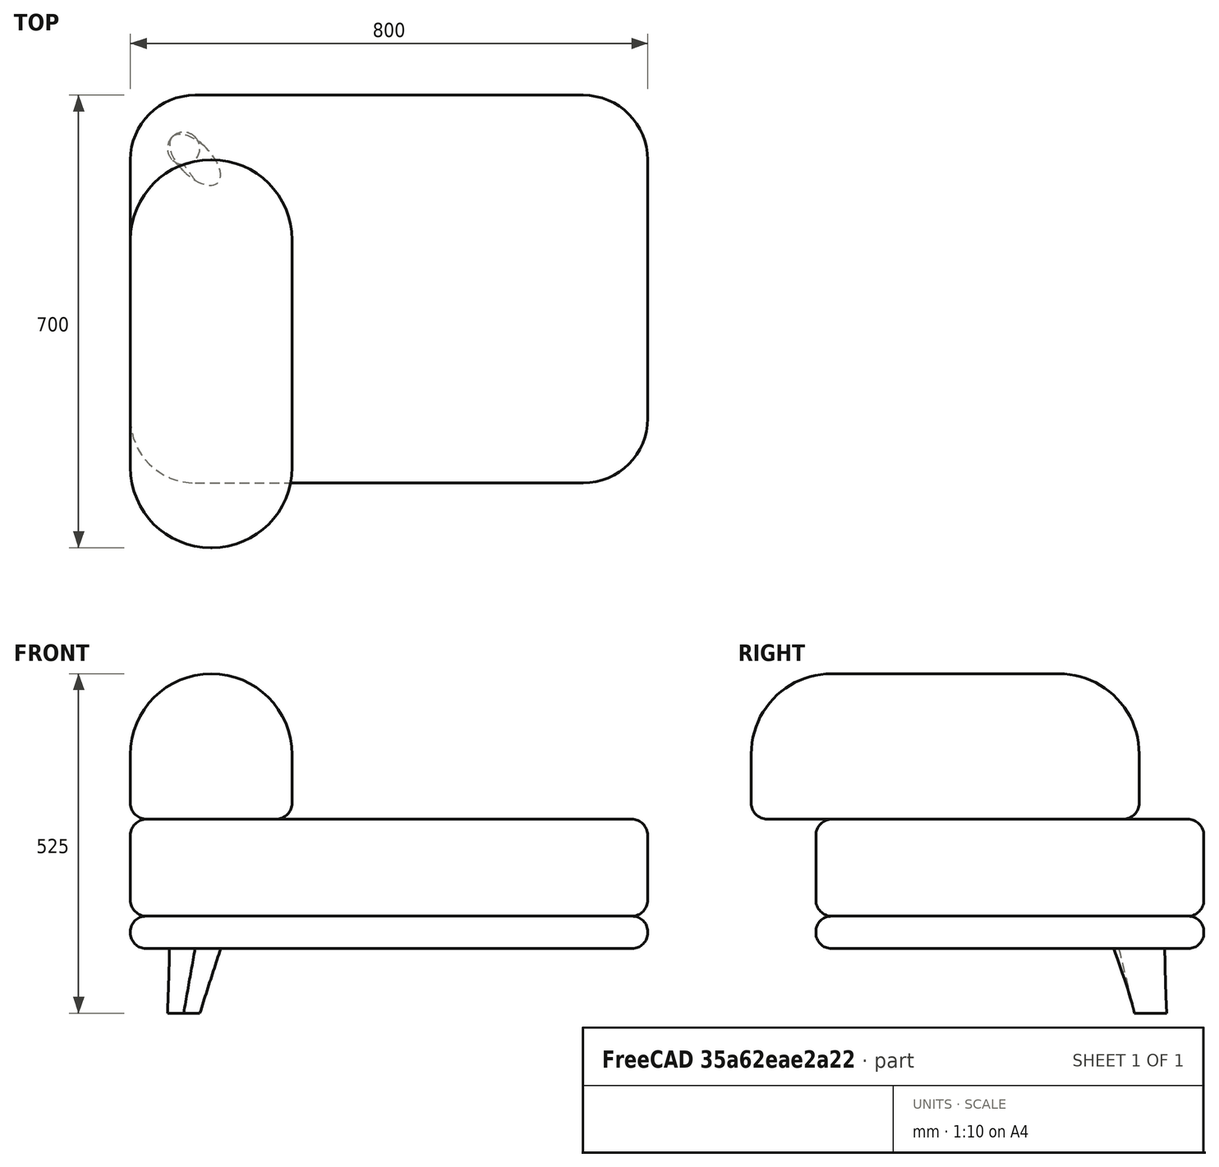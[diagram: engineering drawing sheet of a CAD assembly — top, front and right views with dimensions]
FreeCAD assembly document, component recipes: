
FREECAD ASSEMBLY — COMPONENT RECIPES ("Drawing room Sofa center")

This assembly document has 7 components, labeled P0..P6 below (a component is one placed body or linked part). 7 of them carry a construction recipe — the FreeCAD feature program that regenerates the part from scratch, quoted from this document or its linked companion documents; the rest are supplied as boundary geometry only. No exploded tour is included for this assembly.
COMPONENT P0 — recipe-attached ("Backrest001", modeled in this document).
Construction recipe (the document's own serialized feature program — sketch geometry with constraints, then the solid features built on it; lengths are millimeters unless a unit is written):

FEATURE [Sketcher::SketchObject] Sketch002
  ArcFitTolerance = 1e-06
  AttachmentSupport = -> [XZ_Plane002]
  FullyConstrained = true
  MakeInternals = false
  MapMode = 5
  Placement = pos=(0,0,0) rot=(1,0,0;1.5708rad)
  sketch-geometry (5):
    g0: LineSegment StartX=0 StartY=0 StartZ=0 EndX=250 EndY=0 EndZ=0
    g1: LineSegment StartX=250 StartY=0 StartZ=0 EndX=250 EndY=100 EndZ=0
    g2: LineSegment [constr] StartX=250 StartY=100 StartZ=0 EndX=0 EndY=100 EndZ=0
    g3: LineSegment StartX=0 StartY=100 StartZ=0 EndX=0 EndY=0 EndZ=0
    g4: ArcOfCircle CenterX=125 CenterY=100 CenterZ=0 NormalX=0 NormalY=0 NormalZ=1 AngleXU=0 Radius=125 StartAngle=0 EndAngle=3.14159
  constraints (14):
    c: Coincident(g0,g1)
    c: Coincident(g1,g2)
    c: Coincident(g2,g3)
    c: Coincident(g3,g0)
    c: Horizontal(g0)
    c: Horizontal(g2)
    c: Vertical(g1)
    c: Vertical(g3)
    c: Distance(g1,g3) = 250
    c: Distance(g0,g2) = 100
    c: Coincident(g0,g-1)
    c: Coincident(g4,g2)
    c: Coincident(g4,g1)
    c: PointOnObject(g4,g2)
FEATURE [PartDesign::Pad] Pad002
  Direction = (0,-1,2e-16)
  Length = 600
  Length2 = 10
  Placement = pos=(0,0,0) rot=(1,0,0;1.5708rad)
  Profile = -> Sketch002
  ReferenceAxis = -> Sketch002 [N_Axis]
  Refine = true
  Suppressed = false
  Type = 0
FEATURE [PartDesign::Fillet] Fillet002
  Base = -> Pad002 [Edge9,Edge10]
  BaseFeature = -> Pad002
  Placement = pos=(0,0,0) rot=(1,0,0;1.5708rad)
  Radius = 124
  Refine = true
  SupportTransform = false
  Suppressed = false
  UseAllEdges = false
FEATURE [PartDesign::Fillet] Fillet003
  Base = -> Fillet002 [Face1]
  BaseFeature = -> Fillet002
  Placement = pos=(0,0,0) rot=(1,0,0;1.5708rad)
  Radius = 25
  Refine = true
  SupportTransform = false
  Suppressed = false
  UseAllEdges = true
FEATURE [PartDesign::Body] Body002  label="Backrest"
  AllowCompound = false
  Group = -> [Sketch002,Pad002,Fillet002,Fillet003]
  Origin = -> Origin002
  Placement = pos=(0,-100,200) rot=(0,0,1;0rad)
  Tip = -> Fillet003
COMPONENT P1 — recipe-attached ("Base001", modeled in this document).
Construction recipe (the document's own serialized feature program — sketch geometry with constraints, then the solid features built on it; lengths are millimeters unless a unit is written):

FEATURE [Sketcher::SketchObject] Sketch
  ArcFitTolerance = 1e-06
  AttachmentSupport = -> [XY_Plane]
  FullyConstrained = true
  MakeInternals = false
  MapMode = 5
  sketch-geometry (18):
    g0: LineSegment StartX=0 StartY=-100 StartZ=0 EndX=0 EndY=-500 EndZ=0
    g1: LineSegment StartX=100 StartY=-600 StartZ=0 EndX=700 EndY=-600 EndZ=0
    g2: LineSegment StartX=800 StartY=-500 StartZ=0 EndX=800 EndY=-100 EndZ=0
    g3: LineSegment StartX=700 StartY=0 StartZ=0 EndX=100 EndY=0 EndZ=0
    g4: ArcOfCircle CenterX=100 CenterY=-100 CenterZ=0 NormalX=0 NormalY=0 NormalZ=1 AngleXU=0 Radius=100 StartAngle=1.5708 EndAngle=3.14159
    g5: ArcOfCircle CenterX=100 CenterY=-500 CenterZ=0 NormalX=0 NormalY=0 NormalZ=1 AngleXU=0 Radius=100 StartAngle=3.14159 EndAngle=4.71239
    g6: ArcOfCircle CenterX=700 CenterY=-500 CenterZ=0 NormalX=0 NormalY=0 NormalZ=1 AngleXU=0 Radius=100 StartAngle=4.71239 EndAngle=6.28319
    g7: ArcOfCircle CenterX=700 CenterY=-100 CenterZ=0 NormalX=0 NormalY=0 NormalZ=1 AngleXU=0 Radius=100 StartAngle=0 EndAngle=1.5708
    g8: LineSegment [constr] StartX=25 StartY=-100 StartZ=0 EndX=25 EndY=-500 EndZ=0
    g9: LineSegment [constr] StartX=100 StartY=-575 StartZ=0 EndX=700 EndY=-575 EndZ=0
    g10: LineSegment [constr] StartX=775 StartY=-500 StartZ=0 EndX=775 EndY=-100 EndZ=0
    g11: LineSegment [constr] StartX=700 StartY=-25 StartZ=0 EndX=100 EndY=-25 EndZ=0
    g12: ArcOfCircle [constr] CenterX=100 CenterY=-100 CenterZ=0 NormalX=0 NormalY=0 NormalZ=1 AngleXU=0 Radius=75 StartAngle=1.5708 EndAngle=3.14159
    g13: ArcOfCircle [constr] CenterX=100 CenterY=-500 CenterZ=0 NormalX=0 NormalY=0 NormalZ=1 AngleXU=0 Radius=75 StartAngle=3.14159 EndAngle=4.71239
    g14: ArcOfCircle [constr] CenterX=700 CenterY=-500 CenterZ=0 NormalX=0 NormalY=0 NormalZ=1 AngleXU=0 Radius=75 StartAngle=4.71239 EndAngle=6.28319
    g15: ArcOfCircle [constr] CenterX=700 CenterY=-100 CenterZ=0 NormalX=0 NormalY=0 NormalZ=1 AngleXU=0 Radius=75 StartAngle=0 EndAngle=1.5708
    g16: GeomPoint [constr] X=0 Y=0 Z=0
    g17: GeomPoint [constr] X=800 Y=-600 Z=0
  constraints (39):
    c: Tangent(g0,g4) = -1.5708
    c: Tangent(g0,g5) = -1.5708
    c: Tangent(g1,g5) = -1.5708
    c: Tangent(g1,g6) = -1.5708
    c: Tangent(g2,g6) = -1.5708
    c: Tangent(g2,g7) = -1.5708
    c: Tangent(g3,g7) = -1.5708
    c: Tangent(g3,g4) = -1.5708
    c: Vertical(g0)
    c: Vertical(g2)
    c: Horizontal(g1)
    c: Horizontal(g3)
    c: Equal(g4,g5)
    c: Equal(g5,g6)
    c: Equal(g6,g7)
    c: Tangent(g8,g12) = -1.5708
    c: Tangent(g8,g13) = -1.5708
    c: Tangent(g9,g13) = -1.5708
    c: Tangent(g9,g14) = -1.5708
    c: Tangent(g10,g14) = -1.5708
    c: Tangent(g10,g15) = -1.5708
    c: Tangent(g11,g15) = -1.5708
    c: Tangent(g11,g12) = -1.5708
    c: Coincident(g4,g12)
    c: Coincident(g5,g13)
    c: Coincident(g6,g14)
    c: Coincident(g7,g15)
    c: Vertical(g8)
    c: Vertical(g10)
    c: Horizontal(g9)
    c: PointOnObject(g16,g0)
    c: PointOnObject(g16,g3)
    c: PointOnObject(g17,g1)
    c: PointOnObject(g17,g2)
    c: Distance(g0,g2) = 800
    c: Distance(g1,g3) = 600
    c: Radius(g5) = 100
    c: Distance(g8,g0) = 25
    c: Coincident(g16,g-1)
FEATURE [PartDesign::Pad] Pad
  Direction = (0,0,1)
  Length = 50
  Length2 = 10
  Profile = -> Sketch
  ReferenceAxis = -> Sketch [N_Axis]
  Refine = true
  Suppressed = false
  Type = 0
FEATURE [PartDesign::Fillet] Fillet001
  Base = -> Pad [Face10]
  BaseFeature = -> Pad
  Radius = 24
  Refine = true
  SupportTransform = false
  Suppressed = false
  UseAllEdges = true
FEATURE [PartDesign::Body] Body  label="Base"
  AllowCompound = false
  Group = -> [Sketch,Pad,Fillet001]
  Origin = -> Origin
  Tip = -> Fillet001
COMPONENT P2 — recipe-attached ("Cushion001", modeled in this document).
Construction recipe (the document's own serialized feature program — sketch geometry with constraints, then the solid features built on it; lengths are millimeters unless a unit is written):

FEATURE [Sketcher::SketchObject] Sketch001
  ArcFitTolerance = 1e-06
  AttachmentSupport = -> [XY_Plane001]
  FullyConstrained = true
  MakeInternals = false
  MapMode = 5
  sketch-geometry (10):
    g0: LineSegment StartX=6.963e-13 StartY=-100 StartZ=0 EndX=6.963e-13 EndY=-500 EndZ=0
    g1: LineSegment StartX=100 StartY=-600 StartZ=0 EndX=700 EndY=-600 EndZ=0
    g2: LineSegment StartX=800 StartY=-500 StartZ=0 EndX=800 EndY=-100 EndZ=0
    g3: LineSegment StartX=700 StartY=-8.242e-13 StartZ=0 EndX=100 EndY=-8.242e-13 EndZ=0
    g4: ArcOfCircle CenterX=100 CenterY=-100 CenterZ=0 NormalX=0 NormalY=0 NormalZ=1 AngleXU=0 Radius=100 StartAngle=1.5708 EndAngle=3.14159
    g5: ArcOfCircle CenterX=100 CenterY=-500 CenterZ=0 NormalX=0 NormalY=0 NormalZ=1 AngleXU=0 Radius=100 StartAngle=3.14159 EndAngle=4.71239
    g6: ArcOfCircle CenterX=700 CenterY=-500 CenterZ=0 NormalX=0 NormalY=0 NormalZ=1 AngleXU=0 Radius=100 StartAngle=4.71239 EndAngle=6.28319
    g7: ArcOfCircle CenterX=700 CenterY=-100 CenterZ=0 NormalX=0 NormalY=0 NormalZ=1 AngleXU=0 Radius=100 StartAngle=7e-14 EndAngle=1.5708
    g8: GeomPoint [constr] X=0 Y=0 Z=0
    g9: GeomPoint [constr] X=800 Y=-600 Z=0
  constraints (23):
    c: Tangent(g0,g4) = -1.5708
    c: Tangent(g0,g5) = -1.5708
    c: Tangent(g1,g5) = -1.5708
    c: Tangent(g1,g6) = -1.5708
    c: Tangent(g2,g6) = -1.5708
    c: Tangent(g2,g7) = -1.5708
    c: Tangent(g3,g7) = -1.5708
    c: Tangent(g3,g4) = -1.5708
    c: Vertical(g0)
    c: Vertical(g2)
    c: Horizontal(g1)
    c: Horizontal(g3)
    c: Equal(g4,g5)
    c: Equal(g5,g6)
    c: Equal(g6,g7)
    c: PointOnObject(g8,g0)
    c: PointOnObject(g8,g3)
    c: PointOnObject(g9,g1)
    c: PointOnObject(g9,g2)
    c: Distance(g0,g2) = 800
    c: Distance(g1,g3) = 600
    c: Radius(g5) = 100
    c: Coincident(g8,g-1)
FEATURE [PartDesign::Pad] Pad001
  Direction = (0,0,1)
  Length = 150
  Length2 = 10
  Profile = -> Sketch001
  ReferenceAxis = -> Sketch001 [N_Axis]
  Refine = true
  Suppressed = false
  Type = 0
FEATURE [PartDesign::Fillet] Fillet
  Base = -> Pad001 [Edge16,Edge19,Edge22,Edge24,Edge4,Edge7,Edge10,Edge13,Edge21,Edge23,Edge3,Edge6,Edge9,Edge12,Edge15,Edge18]
  BaseFeature = -> Pad001
  Radius = 25
  Refine = true
  SupportTransform = false
  Suppressed = false
  UseAllEdges = false
FEATURE [PartDesign::Body] Body001  label="Cushion"
  AllowCompound = false
  Group = -> [Sketch001,Pad001,Fillet]
  Origin = -> Origin001
  Placement = pos=(0,0,50) rot=(0,0,1;0rad)
  Tip = -> Fillet
COMPONENT P3 — recipe-attached ("Legs001", modeled in this document).
Construction recipe (the document's own serialized feature program — sketch geometry with constraints, then the solid features built on it; lengths are millimeters unless a unit is written):

FEATURE [Sketcher::SketchObject] Sketch003
  ArcFitTolerance = 1e-06
  AttachmentSupport = -> [XY_Plane003]
  FullyConstrained = true
  MakeInternals = false
  MapMode = 5
  sketch-geometry (5):
    g0: Ellipse CenterX=0 CenterY=0 CenterZ=0 NormalX=0 NormalY=0 NormalZ=1 MajorRadius=50 MinorRadius=25 AngleXU=-2.35619
    g1: LineSegment [constr] StartX=-35.3553 StartY=-35.3553 StartZ=0 EndX=35.3553 EndY=35.3553 EndZ=0
    g2: LineSegment [constr] StartX=17.6777 StartY=-17.6777 StartZ=0 EndX=-17.6777 EndY=17.6777 EndZ=0
    g3: GeomPoint [constr] X=-30.6186 Y=-30.6186 Z=0
    g4: GeomPoint [constr] X=30.6186 Y=30.6186 Z=0
  constraints (5):
    c: InternalAlignment(g1-g4 -> g0) x4
    c: Distance(g0,g1) = 50
    c: Angle(g1) = 0.785398
    c: Distance(g0,g2) = 25
    c: Coincident(g0,g-1)
FEATURE [PartDesign::Plane] DatumPlane
  AttachmentOffset = pos=(0,0,-100) rot=(0,0,1;0rad)
  AttachmentSupport = -> [Sketch003]
  Length = 60
  MapMode = 2
  Placement = pos=(0,0,-100) rot=(0,0,1;0rad)
  ResizeMode = 0
  Width = 60
FEATURE [Sketcher::SketchObject] Sketch004
  ArcFitTolerance = 1e-06
  AttachmentSupport = -> [DatumPlane]
  FullyConstrained = true
  MakeInternals = false
  MapMode = 5
  Placement = pos=(0,0,-100) rot=(0,0,1;0rad)
  sketch-geometry (2):
    g0: Circle CenterX=-17.6777 CenterY=-17.6777 CenterZ=0 NormalX=0 NormalY=0 NormalZ=1 AngleXU=0 Radius=25
    g1: LineSegment [constr] StartX=-17.6777 StartY=-17.6777 StartZ=0 EndX=2.4e-15 EndY=4.5e-15 EndZ=0
  constraints (5):
    c: Diameter(g0) = 50
    c: Coincident(g1,g0)
    c: Coincident(g1,g-1)
    c: Angle(g1,g-1) = 2.35619
    c: PointOnObject(g1,g0)
FEATURE [PartDesign::AdditiveLoft] AdditiveLoft
  Closed = false
  Profile = -> Sketch003
  Refine = true
  Ruled = false
  Sections = -> [Sketch004]
  Suppressed = false
FEATURE [PartDesign::Body] Body003  label="Legs"
  AllowCompound = false
  Group = -> [Sketch003,DatumPlane,Sketch004,AdditiveLoft]
  Origin = -> Origin003
  Placement = pos=(100,-100,0) rot=(0,0,1;-1.5708rad)
  Tip = -> AdditiveLoft
COMPONENT P4 — same part as P3; its construction recipe is shown at P3.
COMPONENT P5 — same part as P3; its construction recipe is shown at P3.
COMPONENT P6 — same part as P3; its construction recipe is shown at P3.
PROVENANCE & LICENSES
A FreeCAD (.FCStd) document from a public repository crawl; recipes are the document's own serialized feature recipes (and, for linked parts, companion documents' recipes).
License: as declared in the source repository (recorded in the dataset sidecar).
